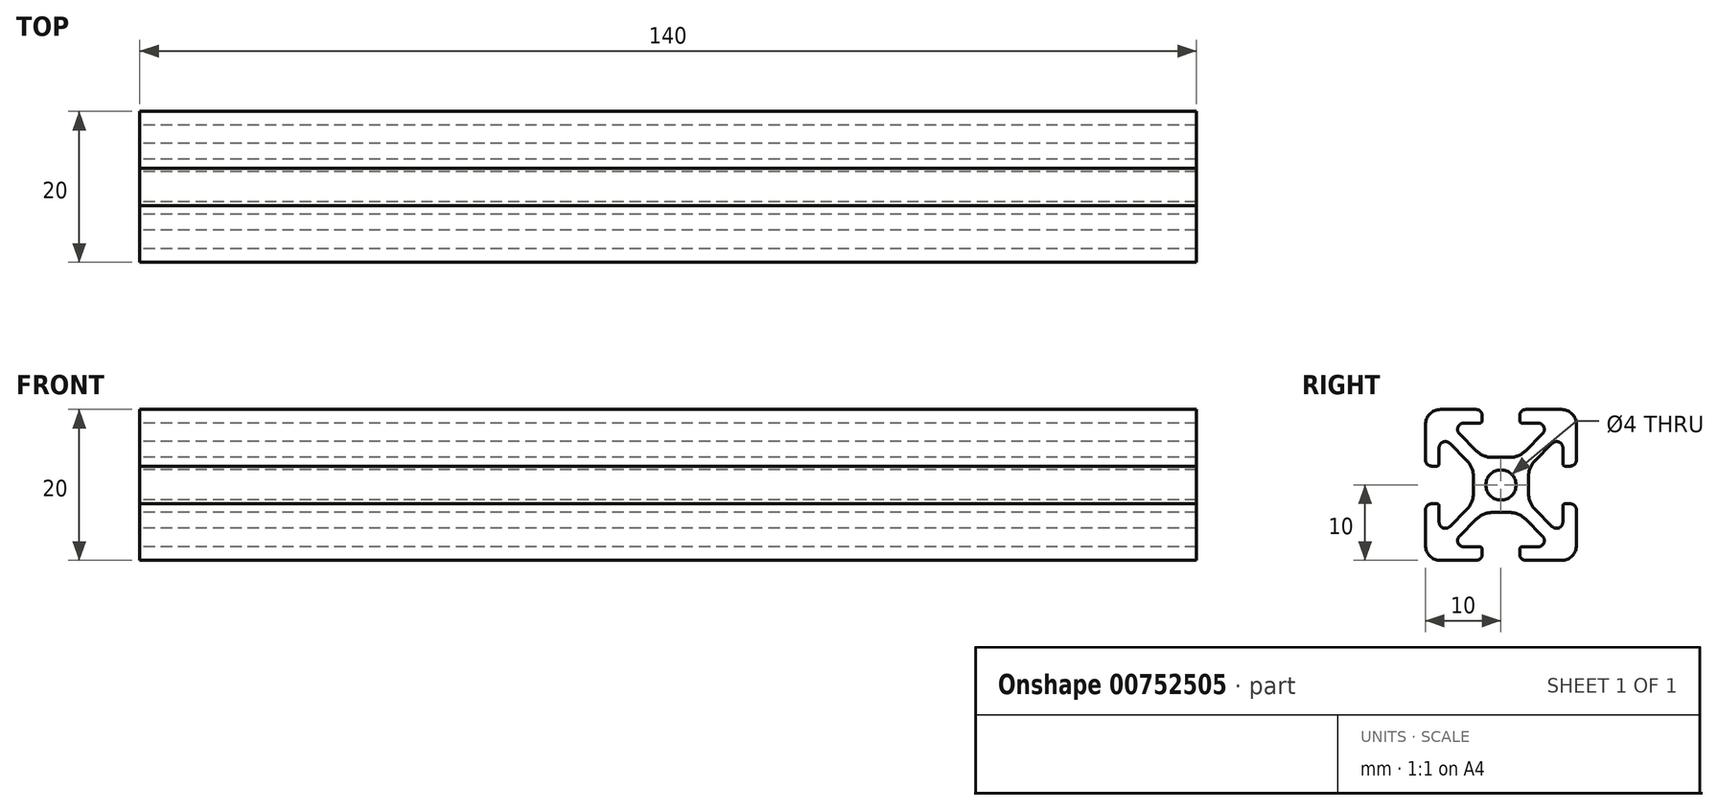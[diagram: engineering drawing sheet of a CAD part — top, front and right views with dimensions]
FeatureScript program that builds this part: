
annotation { "Feature Type Name" : "Feature", "Feature Type Description" : "" }
export const myFeature = defineFeature(function(context is Context, id is Id, definition is map)
    precondition{}
    {
        {
            var Q0;
            Q0=qCreatedBy(makeId("Right.planeOp"),FACE);
            var sketch = newSketch(context, id + "F0", { "sketchPlane" : qUnion([Q0])});
            skLineSegment(sketch, "E0.bottom", {"start": v(-8, 10) * mm, "end": v(-3.3, 10) * mm});
            skLineSegment(sketch, "E0.top", {"start": v(-8, -10) * mm, "end": v(-3.3, -10) * mm});
            skLineSegment(sketch, "E0.right", {"start": v(10, 8) * mm, "end": v(10, 3.3) * mm});
            skLineSegment(sketch, "E1", {"start": v(0, 31.7) * mm, "end": v(0, -24.01) * mm, "construction": true});
            skLineSegment(sketch, "E2", {"start": v(-29.71, 0) * mm, "end": v(21.95, 0) * mm, "construction": true});
            skLineSegment(sketch, "E3", {"start": v(-2.5, 9.2) * mm, "end": v(-2.5, 8.5) * mm});
            skLineSegment(sketch, "E4", {"start": v(-2.8, 8.2) * mm, "end": v(-4.92, 8.2) * mm});
            skLineSegment(sketch, "E5", {"start": v(-5.5, 6.78) * mm, "end": v(-3.25, 4.53) * mm});
            skLineSegment(sketch, "E6", {"start": v(-1.13, 3.65) * mm, "end": v(1.14, 3.65) * mm});
            skLineSegment(sketch, "E7", {"start": v(3.25, 4.53) * mm, "end": v(5.5, 6.78) * mm});
            skLineSegment(sketch, "E8", {"start": v(4.92, 8.2) * mm, "end": v(2.8, 8.2) * mm});
            skLineSegment(sketch, "E9", {"start": v(2.5, 8.5) * mm, "end": v(2.5, 9.2) * mm});
            skLineSegment(sketch, "E10.trimOffspring", {"start": v(3.3, 10) * mm, "end": v(8, 10) * mm});
            skArc(sketch, "E11.filletArc", {"start": v(-8, 10) * mm, "mid": v(-9.41, 9.41) * mm, "end": v(-10, 8) * mm});
            skArc(sketch, "E12.filletArc", {"start": v(-10, -8) * mm, "mid": v(-9.41, -9.41) * mm, "end": v(-8, -10) * mm});
            skArc(sketch, "E13.filletArc", {"start": v(8, -10) * mm, "mid": v(9.41, -9.41) * mm, "end": v(10, -8) * mm});
            skArc(sketch, "E14.filletArc", {"start": v(10, 8) * mm, "mid": v(9.41, 9.41) * mm, "end": v(8, 10) * mm});
            skPoint(sketch, "E15.visualSharp", {"position": v(-9.03, 10.3) * mm});
            skArc(sketch, "E15.filletArc", {"start": v(-4.92, 8.2) * mm, "mid": v(-5.69, 7.69) * mm, "end": v(-5.5, 6.78) * mm});
            skPoint(sketch, "E16.visualSharp", {"position": v(-2.37, 3.65) * mm});
            skArc(sketch, "E16.filletArc", {"start": v(-3.25, 4.53) * mm, "mid": v(-2.28, 3.88) * mm, "end": v(-1.13, 3.65) * mm});
            skPoint(sketch, "E17.visualSharp", {"position": v(2.37, 3.65) * mm});
            skArc(sketch, "E17.filletArc", {"start": v(1.14, 3.65) * mm, "mid": v(2.28, 3.88) * mm, "end": v(3.25, 4.53) * mm});
            skArc(sketch, "E18.filletArc", {"start": v(5.5, 6.78) * mm, "mid": v(5.69, 7.69) * mm, "end": v(4.92, 8.2) * mm});
            skPoint(sketch, "E19.visualSharp", {"position": v(2.5, 8.2) * mm});
            skArc(sketch, "E19.filletArc", {"start": v(2.5, 8.5) * mm, "mid": v(2.59, 8.29) * mm, "end": v(2.8, 8.2) * mm});
            skPoint(sketch, "E20.visualSharp", {"position": v(-2.5, 8.2) * mm});
            skArc(sketch, "E20.filletArc", {"start": v(-2.8, 8.2) * mm, "mid": v(-2.59, 8.29) * mm, "end": v(-2.5, 8.5) * mm});
            skPoint(sketch, "E21.1.5", {"position": v(-3.65, 2.37) * mm});
            skPoint(sketch, "E21.1.13", {"position": v(-10.3, 9.03) * mm});
            skPoint(sketch, "E21.center", {"position": v(0, 0) * mm});
            skLineSegment(sketch, "E22.trimOffspring", {"start": v(-10, -3.3) * mm, "end": v(-10, -8) * mm});
            skLineSegment(sketch, "E23.trimOffspring", {"start": v(10, -3.3) * mm, "end": v(10, -8) * mm});
            skLineSegment(sketch, "E24.trimOffspring", {"start": v(3.3, -10) * mm, "end": v(8, -10) * mm});
            skLineSegment(sketch, "E25", {"start": v(-10, 8) * mm, "end": v(-10, 3.3) * mm});
            skCircle(sketch, "E26", {"center": v(0, 0) * mm, "radius": 2 * mm});
            skPoint(sketch, "E27.visualSharp", {"position": v(-2.5, 10) * mm});
            skArc(sketch, "E27.filletArc", {"start": v(-2.5, 9.2) * mm, "mid": v(-2.73, 9.77) * mm, "end": v(-3.3, 10) * mm});
            skPoint(sketch, "E28.visualSharp", {"position": v(2.5, 10) * mm});
            skArc(sketch, "E28.filletArc", {"start": v(3.3, 10) * mm, "mid": v(2.73, 9.77) * mm, "end": v(2.5, 9.2) * mm});
            skPoint(sketch, "E29.1.1", {"position": v(-10, -2.5) * mm});
            skLineSegment(sketch, "E29.1.2", {"start": v(-3.65, -1.13) * mm, "end": v(-3.65, 1.14) * mm});
            skArc(sketch, "E29.1.3", {"start": v(-4.53, -3.25) * mm, "mid": v(-3.88, -2.28) * mm, "end": v(-3.65, -1.13) * mm});
            skPoint(sketch, "E29.1.4", {"position": v(-8.2, -2.5) * mm});
            skArc(sketch, "E29.1.5", {"start": v(-8.2, -4.92) * mm, "mid": v(-7.69, -5.69) * mm, "end": v(-6.78, -5.5) * mm});
            skLineSegment(sketch, "E29.1.6", {"start": v(-8.2, -2.8) * mm, "end": v(-8.2, -4.92) * mm});
            skLineSegment(sketch, "E29.1.7", {"start": v(-8.2, 4.92) * mm, "end": v(-8.2, 2.8) * mm});
            skArc(sketch, "E29.1.8", {"start": v(-3.65, 1.14) * mm, "mid": v(-3.88, 2.28) * mm, "end": v(-4.53, 3.25) * mm});
            skArc(sketch, "E29.1.9", {"start": v(-6.78, 5.5) * mm, "mid": v(-7.69, 5.69) * mm, "end": v(-8.2, 4.92) * mm});
            skPoint(sketch, "E29.1.10", {"position": v(-3.65, -2.37) * mm});
            skPoint(sketch, "E29.1.11", {"position": v(-10, 2.5) * mm});
            skPoint(sketch, "E29.1.12", {"position": v(-8.2, 2.5) * mm});
            skLineSegment(sketch, "E29.1.13", {"start": v(-6.78, -5.5) * mm, "end": v(-4.53, -3.25) * mm});
            skLineSegment(sketch, "E29.1.14", {"start": v(-4.53, 3.25) * mm, "end": v(-6.78, 5.5) * mm});
            skArc(sketch, "E29.1.15", {"start": v(-10, 3.3) * mm, "mid": v(-9.77, 2.73) * mm, "end": v(-9.2, 2.5) * mm});
            skArc(sketch, "E29.1.16", {"start": v(-9.2, -2.5) * mm, "mid": v(-9.77, -2.73) * mm, "end": v(-10, -3.3) * mm});
            skLineSegment(sketch, "E29.1.17", {"start": v(-8.5, 2.5) * mm, "end": v(-9.2, 2.5) * mm});
            skLineSegment(sketch, "E29.1.18", {"start": v(-9.2, -2.5) * mm, "end": v(-8.5, -2.5) * mm});
            skArc(sketch, "E29.1.19", {"start": v(-8.2, -2.8) * mm, "mid": v(-8.29, -2.59) * mm, "end": v(-8.5, -2.5) * mm});
            skArc(sketch, "E29.1.20", {"start": v(-8.5, 2.5) * mm, "mid": v(-8.29, 2.59) * mm, "end": v(-8.2, 2.8) * mm});
            skPoint(sketch, "E29.2.0", {"position": v(-2.37, -3.65) * mm});
            skPoint(sketch, "E29.2.1", {"position": v(2.5, -10) * mm});
            skLineSegment(sketch, "E29.2.2", {"start": v(1.13, -3.65) * mm, "end": v(-1.14, -3.65) * mm});
            skArc(sketch, "E29.2.3", {"start": v(3.25, -4.53) * mm, "mid": v(2.28, -3.88) * mm, "end": v(1.13, -3.65) * mm});
            skPoint(sketch, "E29.2.4", {"position": v(2.5, -8.2) * mm});
            skArc(sketch, "E29.2.5", {"start": v(4.92, -8.2) * mm, "mid": v(5.69, -7.69) * mm, "end": v(5.5, -6.78) * mm});
            skLineSegment(sketch, "E29.2.6", {"start": v(2.8, -8.2) * mm, "end": v(4.92, -8.2) * mm});
            skLineSegment(sketch, "E29.2.7", {"start": v(-4.92, -8.2) * mm, "end": v(-2.8, -8.2) * mm});
            skArc(sketch, "E29.2.8", {"start": v(-1.14, -3.65) * mm, "mid": v(-2.28, -3.88) * mm, "end": v(-3.25, -4.53) * mm});
            skArc(sketch, "E29.2.9", {"start": v(-5.5, -6.78) * mm, "mid": v(-5.69, -7.69) * mm, "end": v(-4.92, -8.2) * mm});
            skPoint(sketch, "E29.2.10", {"position": v(2.37, -3.65) * mm});
            skPoint(sketch, "E29.2.11", {"position": v(-2.5, -10) * mm});
            skPoint(sketch, "E29.2.12", {"position": v(-2.5, -8.2) * mm});
            skLineSegment(sketch, "E29.2.13", {"start": v(5.5, -6.78) * mm, "end": v(3.25, -4.53) * mm});
            skLineSegment(sketch, "E29.2.14", {"start": v(-3.25, -4.53) * mm, "end": v(-5.5, -6.78) * mm});
            skArc(sketch, "E29.2.15", {"start": v(-3.3, -10) * mm, "mid": v(-2.73, -9.77) * mm, "end": v(-2.5, -9.2) * mm});
            skArc(sketch, "E29.2.16", {"start": v(2.5, -9.2) * mm, "mid": v(2.73, -9.77) * mm, "end": v(3.3, -10) * mm});
            skLineSegment(sketch, "E29.2.17", {"start": v(-2.5, -8.5) * mm, "end": v(-2.5, -9.2) * mm});
            skLineSegment(sketch, "E29.2.18", {"start": v(2.5, -9.2) * mm, "end": v(2.5, -8.5) * mm});
            skArc(sketch, "E29.2.19", {"start": v(2.8, -8.2) * mm, "mid": v(2.59, -8.29) * mm, "end": v(2.5, -8.5) * mm});
            skArc(sketch, "E29.2.20", {"start": v(-2.5, -8.5) * mm, "mid": v(-2.59, -8.29) * mm, "end": v(-2.8, -8.2) * mm});
            skPoint(sketch, "E29.3.0", {"position": v(3.65, -2.37) * mm});
            skPoint(sketch, "E29.3.1", {"position": v(10, 2.5) * mm});
            skLineSegment(sketch, "E29.3.2", {"start": v(3.65, 1.13) * mm, "end": v(3.65, -1.14) * mm});
            skArc(sketch, "E29.3.3", {"start": v(4.53, 3.25) * mm, "mid": v(3.88, 2.28) * mm, "end": v(3.65, 1.13) * mm});
            skPoint(sketch, "E29.3.4", {"position": v(8.2, 2.5) * mm});
            skArc(sketch, "E29.3.5", {"start": v(8.2, 4.92) * mm, "mid": v(7.69, 5.69) * mm, "end": v(6.78, 5.5) * mm});
            skLineSegment(sketch, "E29.3.6", {"start": v(8.2, 2.8) * mm, "end": v(8.2, 4.92) * mm});
            skLineSegment(sketch, "E29.3.7", {"start": v(8.2, -4.92) * mm, "end": v(8.2, -2.8) * mm});
            skArc(sketch, "E29.3.8", {"start": v(3.65, -1.14) * mm, "mid": v(3.88, -2.28) * mm, "end": v(4.53, -3.25) * mm});
            skArc(sketch, "E29.3.9", {"start": v(6.78, -5.5) * mm, "mid": v(7.69, -5.69) * mm, "end": v(8.2, -4.92) * mm});
            skPoint(sketch, "E29.3.10", {"position": v(3.65, 2.37) * mm});
            skPoint(sketch, "E29.3.11", {"position": v(10, -2.5) * mm});
            skPoint(sketch, "E29.3.12", {"position": v(8.2, -2.5) * mm});
            skLineSegment(sketch, "E29.3.13", {"start": v(6.78, 5.5) * mm, "end": v(4.53, 3.25) * mm});
            skLineSegment(sketch, "E29.3.14", {"start": v(4.53, -3.25) * mm, "end": v(6.78, -5.5) * mm});
            skArc(sketch, "E29.3.15", {"start": v(10, -3.3) * mm, "mid": v(9.77, -2.73) * mm, "end": v(9.2, -2.5) * mm});
            skArc(sketch, "E29.3.16", {"start": v(9.2, 2.5) * mm, "mid": v(9.77, 2.73) * mm, "end": v(10, 3.3) * mm});
            skLineSegment(sketch, "E29.3.17", {"start": v(8.5, -2.5) * mm, "end": v(9.2, -2.5) * mm});
            skLineSegment(sketch, "E29.3.18", {"start": v(9.2, 2.5) * mm, "end": v(8.5, 2.5) * mm});
            skArc(sketch, "E29.3.19", {"start": v(8.2, 2.8) * mm, "mid": v(8.29, 2.59) * mm, "end": v(8.5, 2.5) * mm});
            skArc(sketch, "E29.3.20", {"start": v(8.5, -2.5) * mm, "mid": v(8.29, -2.59) * mm, "end": v(8.2, -2.8) * mm});
            skSolve(sketch);
        }
        {
            var Q0;
            Q0=qSketchRegion(id+"F0",true);
            extrude(context, id + "F1", {"entities" : qUnion([Q0]), "depth" : 140 * mm, "offsetDistance" : 25 * mm});
        }
    });
